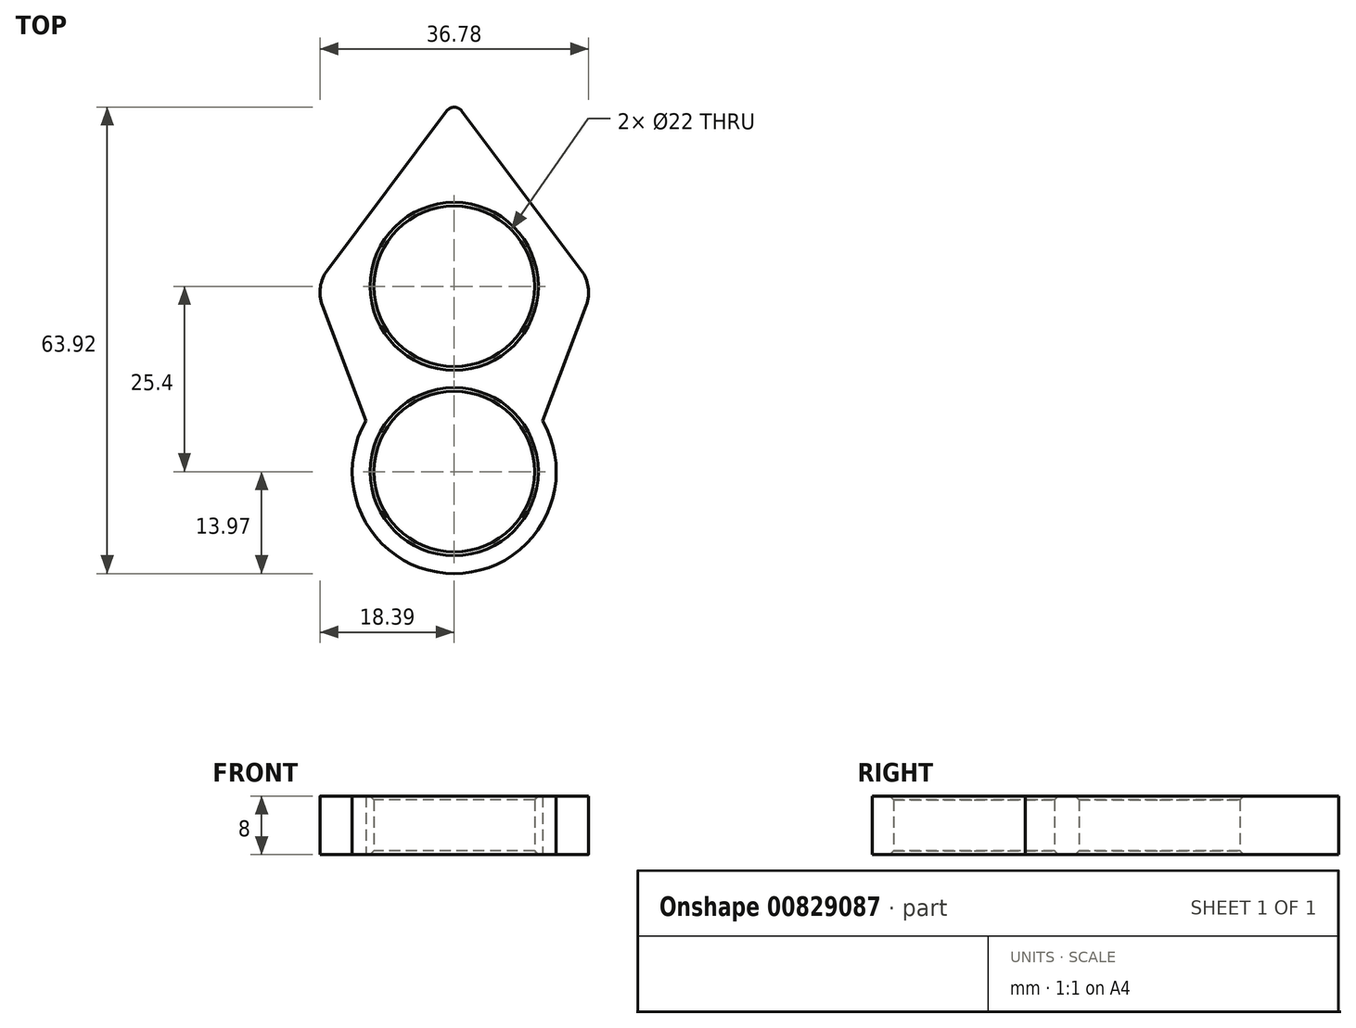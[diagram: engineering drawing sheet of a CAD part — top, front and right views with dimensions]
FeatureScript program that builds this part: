
annotation { "Feature Type Name" : "Feature", "Feature Type Description" : "" }
export const myFeature = defineFeature(function(context is Context, id is Id, definition is map)
    precondition{}
    {
        {
            var Q0;
            Q0=qCreatedBy(makeId("Top.planeOp"),FACE);
            var sketch = newSketch(context, id + "F0", { "sketchPlane" : qUnion([Q0])});
            skCircle(sketch, "E0", {"center": v(0, 0) * mm, "radius": 11 * mm});
            skCircle(sketch, "E1", {"center": v(0, 0) * mm, "radius": 13.97 * mm});
            skCircle(sketch, "E2", {"center": v(0, 0) * mm, "radius": 25.4 * mm, "construction": true});
            skCircle(sketch, "E3", {"center": v(0, 0) * mm, "radius": 50.8 * mm, "construction": true});
            skCircle(sketch, "E4", {"center": v(0, 25.4) * mm, "radius": 11 * mm});
            skLineSegment(sketch, "E5", {"start": v(0, 0) * mm, "end": v(-61.23, 35.35) * mm, "construction": true});
            skLineSegment(sketch, "E6", {"start": v(-12.1, 6.99) * mm, "end": v(-19.05, 25.4) * mm});
            skLineSegment(sketch, "E7", {"start": v(-19.05, 25.4) * mm, "end": v(0, 50.8) * mm});
            skLineSegment(sketch, "E8", {"start": v(0, 50.8) * mm, "end": v(19.05, 25.4) * mm});
            skLineSegment(sketch, "E9", {"start": v(19.05, 25.4) * mm, "end": v(12.1, 6.98) * mm});
            skSolve(sketch);
        }
        {
            var Q0;
            Q0=makeQuery(id+"F0.imprint","IMPRINT",FACE,{"disambiguationData":[TD([[makeQuery(id+"F0.imprint","IMPRINT",EDGE,{"derivedFrom":sQuery(id+"F0.wireOp",EDGE,"E0")}),-1.0]])]});
            extrude(context, id + "F1", {"entities" : qUnion([Q0]), "endBound" : BoundingType.SYMMETRIC, "depth" : 8 * mm, "offsetDistance" : 25.4 * mm});
        }
        {
            var Q0;
            Q0=makeQuery(id+"F0.imprint","IMPRINT",FACE,{"disambiguationData":[TD([[makeQuery(id+"F0.imprint","IMPRINT",EDGE,{"derivedFrom":sQuery(id+"F0.wireOp",EDGE,"E4")}),-1.0]])]});
            extrude(context, id + "F2", {"entities" : qUnion([Q0]), "operationType" : NewBodyOperationType.ADD, "endBound" : BoundingType.SYMMETRIC, "depth" : 8 * mm, "offsetDistance" : 25.4 * mm});
        }
        {
            var Q0;
            {var subQ0=sQuery(id+"F0.wireOp",EDGE,"E1");Q0=makeQuery(id+"FiUzVrOvQGAGDEY_1.2.F2.boolean.opBoolean","MERGE",EDGE,{"derivedFrom":[makeQuery(id+"FiUzVrOvQGAGDEY_1.1.F2.opExtrude","SWEPT_EDGE",EDGE,{"disambiguationData":[OSD([subQ0,sQuery(id+"F0.wireOp",EDGE,"E9")])]}),makeQuery(id+"FiUzVrOvQGAGDEY_1.2.F2.opExtrude","SWEPT_EDGE",EDGE,{"disambiguationData":[OSD([subQ0,sQuery(id+"F0.wireOp",EDGE,"E6")])]})]});}
            var Q1;
            {var subQ0=sQuery(id+"F0.wireOp",EDGE,"E1");Q1=makeQuery(id+"FiUzVrOvQGAGDEY_1.1.F2.boolean.opBoolean","MERGE",EDGE,{"derivedFrom":[makeQuery(id+"F2.opExtrude","SWEPT_EDGE",EDGE,{"disambiguationData":[OSD([subQ0,sQuery(id+"F0.wireOp",EDGE,"E9")])]}),makeQuery(id+"FiUzVrOvQGAGDEY_1.1.F2.opExtrude","SWEPT_EDGE",EDGE,{"disambiguationData":[OSD([subQ0,sQuery(id+"F0.wireOp",EDGE,"E6")])]})]});}
            var Q2;
            {var subQ0=sQuery(id+"F0.wireOp",EDGE,"E1");Q2=makeQuery(id+"FiUzVrOvQGAGDEY_1.2.F2.boolean.opBoolean","MERGE",EDGE,{"derivedFrom":[makeQuery(id+"F2.opExtrude","SWEPT_EDGE",EDGE,{"disambiguationData":[OSD([subQ0,sQuery(id+"F0.wireOp",EDGE,"E6")])]}),makeQuery(id+"FiUzVrOvQGAGDEY_1.2.F2.opExtrude","SWEPT_EDGE",EDGE,{"disambiguationData":[OSD([subQ0,sQuery(id+"F0.wireOp",EDGE,"E9")])]})]});}
            var Q3;
            Q3=makeQuery(id+"F2.opExtrude","SWEPT_EDGE",EDGE,{"disambiguationData":[OSD([sQuery(id+"F0.wireOp",EDGE,"E7"),sQuery(id+"F0.wireOp",EDGE,"E8")])]});
            var Q4;
            Q4=makeQuery(id+"FiUzVrOvQGAGDEY_1.2.F2.opExtrude","SWEPT_EDGE",EDGE,{"disambiguationData":[OSD([sQuery(id+"F0.wireOp",EDGE,"E7"),sQuery(id+"F0.wireOp",EDGE,"E8")])]});
            var Q5;
            Q5=makeQuery(id+"FiUzVrOvQGAGDEY_1.1.F2.opExtrude","SWEPT_EDGE",EDGE,{"disambiguationData":[OSD([sQuery(id+"F0.wireOp",EDGE,"E7"),sQuery(id+"F0.wireOp",EDGE,"E8")])]});
            fillet(context, id + "F3", {"entities" : qUnion([Q0, Q1, Q2, Q3, Q4, Q5]), "radius" : 1.27 * mm, "tangentPropagation" : true, "allowEdgeOverflow" : false});
        }
        {
            var Q0;
            Q0=makeQuery(id+"FiUzVrOvQGAGDEY_1.1.F2.opExtrude","SWEPT_EDGE",EDGE,{"disambiguationData":[OSD([sQuery(id+"F0.wireOp",EDGE,"E6"),sQuery(id+"F0.wireOp",EDGE,"E7")])]});
            var Q1;
            Q1=makeQuery(id+"F2.opExtrude","SWEPT_EDGE",EDGE,{"disambiguationData":[OSD([sQuery(id+"F0.wireOp",EDGE,"E8"),sQuery(id+"F0.wireOp",EDGE,"E9")])]});
            var Q2;
            Q2=makeQuery(id+"F2.opExtrude","SWEPT_EDGE",EDGE,{"disambiguationData":[OSD([sQuery(id+"F0.wireOp",EDGE,"E6"),sQuery(id+"F0.wireOp",EDGE,"E7")])]});
            var Q3;
            Q3=makeQuery(id+"FiUzVrOvQGAGDEY_1.2.F2.opExtrude","SWEPT_EDGE",EDGE,{"disambiguationData":[OSD([sQuery(id+"F0.wireOp",EDGE,"E8"),sQuery(id+"F0.wireOp",EDGE,"E9")])]});
            var Q4;
            Q4=makeQuery(id+"FiUzVrOvQGAGDEY_1.1.F2.opExtrude","SWEPT_EDGE",EDGE,{"disambiguationData":[OSD([sQuery(id+"F0.wireOp",EDGE,"E8"),sQuery(id+"F0.wireOp",EDGE,"E9")])]});
            var Q5;
            Q5=makeQuery(id+"FiUzVrOvQGAGDEY_1.2.F2.opExtrude","SWEPT_EDGE",EDGE,{"disambiguationData":[OSD([sQuery(id+"F0.wireOp",EDGE,"E6"),sQuery(id+"F0.wireOp",EDGE,"E7")])]});
            fillet(context, id + "F4", {"entities" : qUnion([Q0, Q1, Q2, Q3, Q4, Q5]), "radius" : 5.08 * mm, "tangentPropagation" : true, "allowEdgeOverflow" : false});
        }
        {
            var Q0;
            Q0=makeQuery(id+"FiUzVrOvQGAGDEY_1.2.F2.opExtrude","CAP_EDGE",EDGE,{"disambiguationData":[OSD([sQuery(id+"F0.wireOp",EDGE,"E4")])],"isStart":false});
            var Q1;
            Q1=makeQuery(id+"F2.opExtrude","CAP_EDGE",EDGE,{"disambiguationData":[OSD([sQuery(id+"F0.wireOp",EDGE,"E4")])],"isStart":false});
            var Q2;
            Q2=makeQuery(id+"F1.opExtrude","CAP_EDGE",EDGE,{"disambiguationData":[OSD([sQuery(id+"F0.wireOp",EDGE,"E0")])],"isStart":false});
            var Q3;
            Q3=makeQuery(id+"FiUzVrOvQGAGDEY_1.1.F2.opExtrude","CAP_EDGE",EDGE,{"disambiguationData":[OSD([sQuery(id+"F0.wireOp",EDGE,"E4")])],"isStart":false});
            var Q4;
            Q4=makeQuery(id+"FiUzVrOvQGAGDEY_1.1.F2.opExtrude","CAP_EDGE",EDGE,{"disambiguationData":[OSD([sQuery(id+"F0.wireOp",EDGE,"E4")])],"isStart":true});
            var Q5;
            Q5=makeQuery(id+"F1.opExtrude","CAP_EDGE",EDGE,{"disambiguationData":[OSD([sQuery(id+"F0.wireOp",EDGE,"E0")])],"isStart":true});
            var Q6;
            Q6=makeQuery(id+"FiUzVrOvQGAGDEY_1.2.F2.opExtrude","CAP_EDGE",EDGE,{"disambiguationData":[OSD([sQuery(id+"F0.wireOp",EDGE,"E4")])],"isStart":true});
            var Q7;
            Q7=makeQuery(id+"F2.opExtrude","CAP_EDGE",EDGE,{"disambiguationData":[OSD([sQuery(id+"F0.wireOp",EDGE,"E4")])],"isStart":true});
            chamfer(context, id + "F5", {"entities" : qUnion([Q0, Q1, Q2, Q3, Q4, Q5, Q6, Q7]), "width" : 0.5 * mm, "tangentPropagation" : true});
        }
    });
